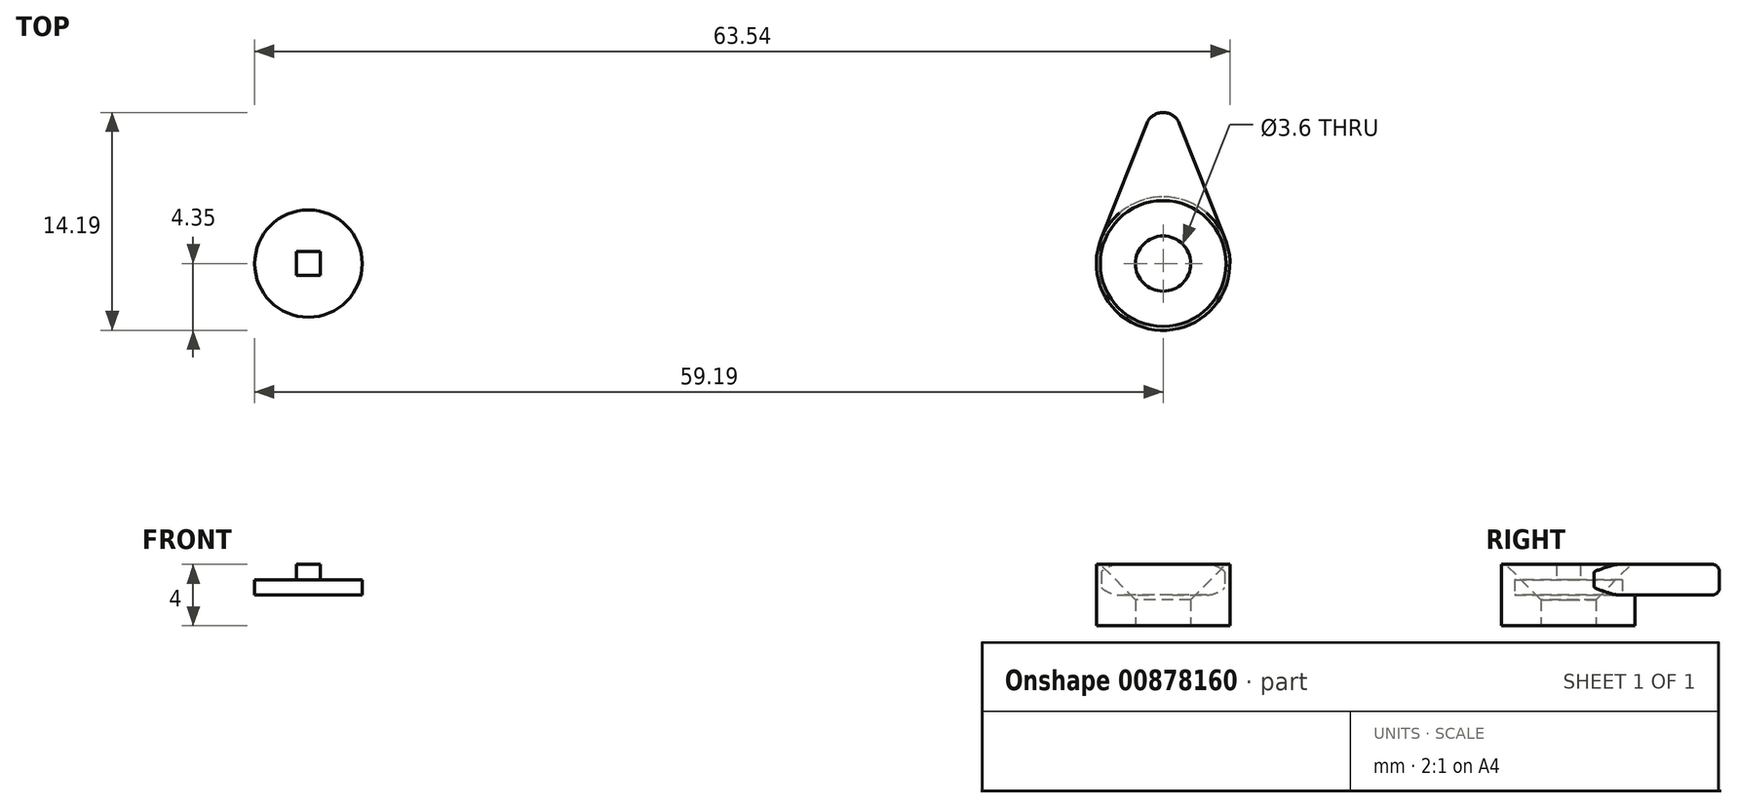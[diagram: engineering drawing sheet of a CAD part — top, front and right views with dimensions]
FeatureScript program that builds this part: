
annotation { "Feature Type Name" : "Feature", "Feature Type Description" : "" }
export const myFeature = defineFeature(function(context is Context, id is Id, definition is map)
    precondition{}
    {
        {
            var Q0;
            Q0=qCreatedBy(makeId("Top.planeOp"),FACE);
            var sketch = newSketch(context, id + "F0", { "sketchPlane" : qUnion([Q0])});
            skCircle(sketch, "E0", {"center": v(0, 0) * mm, "radius": 4.35 * mm});
            skCircle(sketch, "E1", {"center": v(0, 0) * mm, "radius": 1.8 * mm});
            skCircle(sketch, "E2", {"center": v(0, 8.7) * mm, "radius": 1.15 * mm});
            skLineSegment(sketch, "E3", {"start": v(-4.01, 1.68) * mm, "end": v(-1.07, 9.12) * mm});
            skLineSegment(sketch, "E4", {"start": v(1.07, 9.12) * mm, "end": v(4.01, 1.68) * mm});
            skSolve(sketch);
        }
        {
            var Q0;
            {var subQ0=sQuery(id+"F0.wireOp",EDGE,"E3");Q0=makeQuery(id+"F0.imprint","IMPRINT",FACE,{"disambiguationData":[TD([[makeQuery(id+"F0.imprint","IMPRINT",EDGE,{"derivedFrom":subQ0}),-1.0]])]});}
            var Q1;
            {var subQ0=sQuery(id+"F0.wireOp",EDGE,"E2");var subQ1=makeQuery(id+"F0.imprint","INTERSECT",VERTEX,{"derivedFrom":[subQ0,sQuery(id+"F0.wireOp",EDGE,"E3")]});Q1=makeQuery(id+"F0.imprint","IMPRINT",FACE,{"disambiguationData":[TD([[makeQuery(id+"F0.imprint","IMPRINT",EDGE,{"disambiguationData":[TD([[subQ1,1.0]])],"derivedFrom":subQ0}),1.0]])]});}
            var Q2;
            Q2=makeQuery(id+"F0.imprint","IMPRINT",FACE,{"disambiguationData":[TD([[makeQuery(id+"F0.imprint","IMPRINT",EDGE,{"derivedFrom":sQuery(id+"F0.wireOp",EDGE,"E1")}),-1.0]])]});
            extrude(context, id + "F1", {"entities" : qUnion([Q0, Q1, Q2]), "depth" : 2 * mm, "offsetDistance" : 25 * mm});
        }
        {
            var Q0;
            Q0=makeQuery(id+"F0.imprint","IMPRINT",FACE,{"disambiguationData":[TD([[makeQuery(id+"F0.imprint","IMPRINT",EDGE,{"derivedFrom":sQuery(id+"F0.wireOp",EDGE,"E1")}),-1.0]])]});
            extrude(context, id + "F2", {"entities" : qUnion([Q0]), "operationType" : NewBodyOperationType.ADD, "oppositeDirection" : true, "depth" : 2 * mm, "offsetDistance" : 25 * mm});
        }
        {
            var Q0;
            Q0=makeQuery(id+"F1.opExtrude","CAP_EDGE",EDGE,{"disambiguationData":[OSD([sQuery(id+"F0.wireOp",EDGE,"E2")])],"isStart":true});
            var Q1;
            Q1=makeQuery(id+"F1.opExtrude","CAP_EDGE",EDGE,{"disambiguationData":[OSD([sQuery(id+"F0.wireOp",EDGE,"E3")])],"isStart":true});
            var Q2;
            Q2=makeQuery(id+"F1.opExtrude","CAP_EDGE",EDGE,{"disambiguationData":[OSD([sQuery(id+"F0.wireOp",EDGE,"E3")])],"isStart":false});
            fillet(context, id + "F3", {"entities" : qUnion([Q0, Q1, Q2]), "radius" : 0.5 * mm, "tangentPropagation" : true, "allowEdgeOverflow" : false});
        }
        {
            var Q0;
            Q0=makeQuery(id+"F1.opExtrude","CAP_EDGE",EDGE,{"disambiguationData":[OSD([sQuery(id+"F0.wireOp",EDGE,"E1")])],"isStart":false});
            chamfer(context, id + "F4", {"entities" : qUnion([Q0]), "width" : 2.3 * mm, "tangentPropagation" : true});
        }
        {
            var Q0;
            Q0=qCreatedBy(makeId("Top.planeOp"),FACE);
            var sketch = newSketch(context, id + "F5", { "sketchPlane" : qUnion([Q0])});
            skCircle(sketch, "E5", {"center": v(-55.7, 0) * mm, "radius": 3.5 * mm});
            skSolve(sketch);
        }
        {
            var Q0;
            Q0=makeQuery(id+"F5.imprint","IMPRINT",FACE,{"disambiguationData":[TD([[makeQuery(id+"F5.imprint","IMPRINT",EDGE,{"derivedFrom":sQuery(id+"F5.wireOp",EDGE,"E5")}),1.0]])]});
            extrude(context, id + "F6", {"entities" : qUnion([Q0]), "depth" : 1 * mm, "offsetDistance" : 25 * mm});
        }
        {
            var Q0;
            Q0=makeQuery(id+"F6.opExtrude","CAP_FACE",FACE,{"disambiguationData":[OSD([sQuery(id+"F5.wireOp",EDGE,"E5")])],"isStart":false});
            var sketch = newSketch(context, id + "F7", { "sketchPlane" : qUnion([Q0])});
            skLineSegment(sketch, "E6.bottom", {"start": v(-56.47, 0.77) * mm, "end": v(-54.92, 0.77) * mm});
            skLineSegment(sketch, "E6.top", {"start": v(-56.47, -0.77) * mm, "end": v(-54.92, -0.77) * mm});
            skLineSegment(sketch, "E6.left", {"start": v(-56.47, 0.77) * mm, "end": v(-56.47, -0.77) * mm});
            skLineSegment(sketch, "E6.right", {"start": v(-54.92, 0.77) * mm, "end": v(-54.92, -0.78) * mm});
            skPoint(sketch, "E7.startSnap0", {"position": v(-54.92, 0) * mm});
            skLineSegment(sketch, "E8", {"start": v(-56.47, 0) * mm, "end": v(-59.2, 0) * mm, "construction": true});
            skLineSegment(sketch, "E9", {"start": v(-55.7, 0.77) * mm, "end": v(-55.7, 3.5) * mm, "construction": true});
            skLineSegment(sketch, "E10", {"start": v(-54.92, 0) * mm, "end": v(-52.2, 0) * mm, "construction": true});
            skSolve(sketch);
        }
        {
            var Q0;
            Q0=makeQuery(id+"F7.imprint","IMPRINT",FACE,{"disambiguationData":[TD([[makeQuery(id+"F7.imprint","IMPRINT",EDGE,{"derivedFrom":sQuery(id+"F7.wireOp",EDGE,"E6.bottom")}),-1.0]])]});
            extrude(context, id + "F8", {"entities" : qUnion([Q0]), "operationType" : NewBodyOperationType.ADD, "depth" : 1 * mm, "offsetDistance" : 25 * mm});
        }
    });
